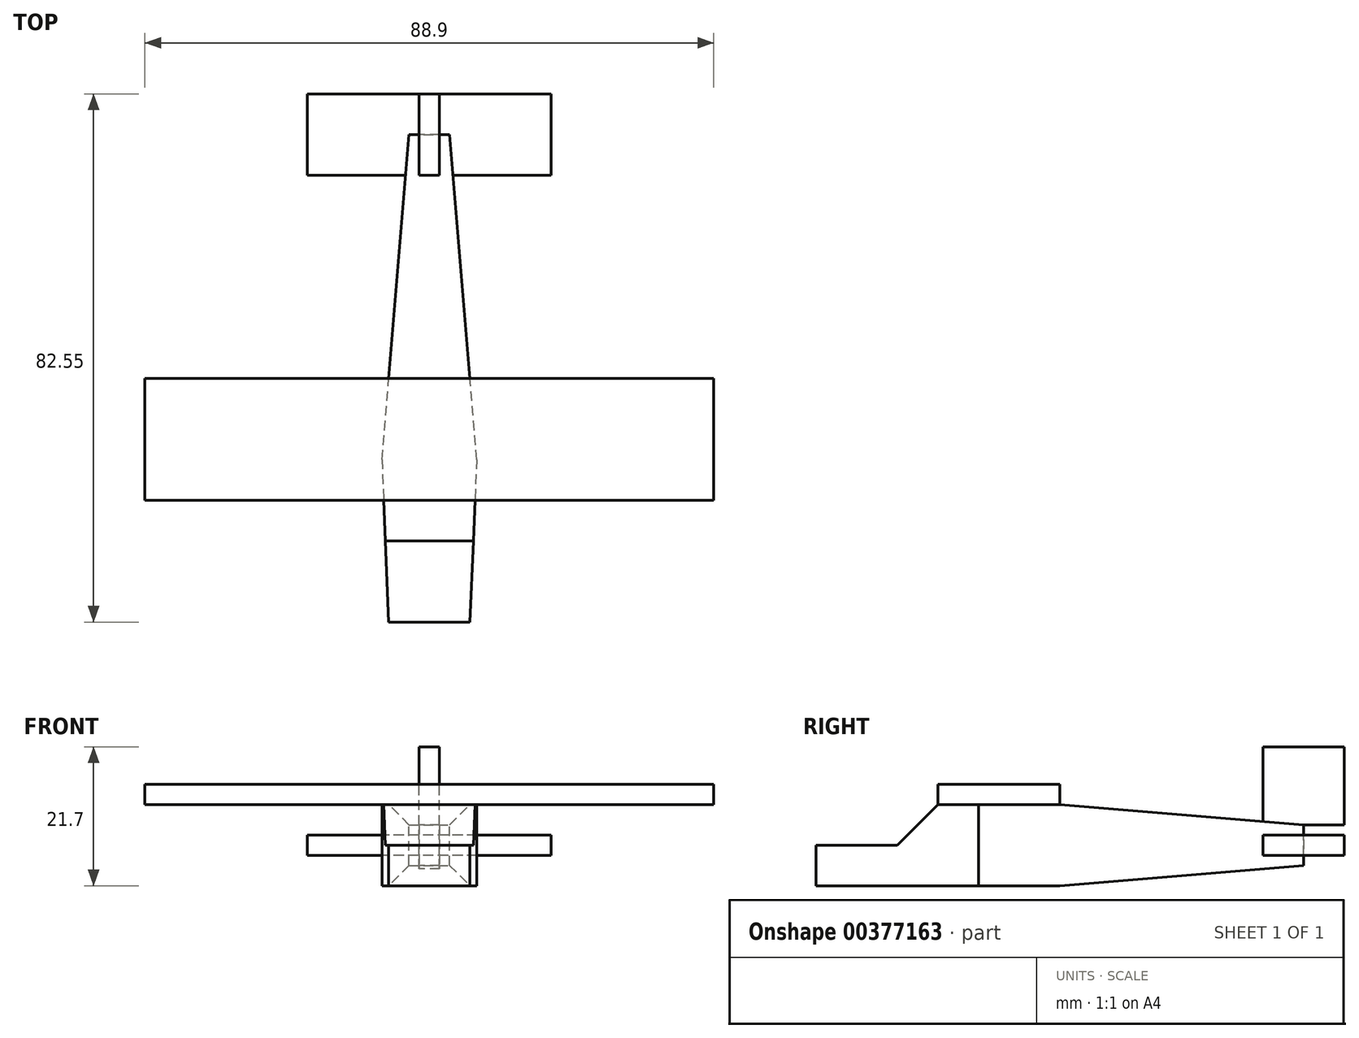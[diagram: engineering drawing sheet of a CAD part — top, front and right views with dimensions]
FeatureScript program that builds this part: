
annotation { "Feature Type Name" : "Feature", "Feature Type Description" : "" }
export const myFeature = defineFeature(function(context is Context, id is Id, definition is map)
    precondition{}
    {
        {
            var Q0;
            Q0=qCreatedBy(makeId("Front.planeOp"),FACE);
            var sketch = newSketch(context, id + "F0", { "sketchPlane" : qUnion([Q0])});
            skLineSegment(sketch, "E0.bottom", {"start": v(9.53, -6.35) * mm, "end": v(-9.53, -6.35) * mm});
            skLineSegment(sketch, "E0.top", {"start": v(9.53, 6.35) * mm, "end": v(-9.53, 6.35) * mm});
            skLineSegment(sketch, "E0.left", {"start": v(9.53, -6.35) * mm, "end": v(9.53, 6.35) * mm});
            skLineSegment(sketch, "E0.right", {"start": v(-9.53, -6.35) * mm, "end": v(-9.53, 6.35) * mm});
            skPoint(sketch, "E0.middle", {"position": v(0, 0) * mm});
            skSolve(sketch);
        }
        {
            var Q0;
            Q0=makeQuery(id+"F0.imprint","IMPRINT",FACE,{"disambiguationData":[TD([[makeQuery(id+"F0.imprint","IMPRINT",EDGE,{"derivedFrom":sQuery(id+"F0.wireOp",EDGE,"E0.bottom")}),-1.0]])]});
            extrude(context, id + "F1", {"entities" : qUnion([Q0]), "depth" : 25.4 * mm, "hasSecondDirection" : true, "secondDirectionOppositeDirection" : true, "secondDirectionDepth" : 50.8 * mm});
        }
        {
            var Q0;
            Q0=makeQuery(id+"F1.opExtrude","SWEPT_FACE",FACE,{"disambiguationData":[OSD([sQuery(id+"F0.wireOp",EDGE,"E0.top")])]});
            var sketch = newSketch(context, id + "F2", { "sketchPlane" : qUnion([Q0])});
            skLineSegment(sketch, "E1", {"start": v(-9.53, -25.4) * mm, "end": v(-3.17, 50.8) * mm});
            skLineSegment(sketch, "E2", {"start": v(-3.17, 50.8) * mm, "end": v(0, 50.8) * mm});
            skLineSegment(sketch, "E3", {"start": v(-9.53, -25.4) * mm, "end": v(0, -25.4) * mm});
            skLineSegment(sketch, "E4.MirrorCS", {"start": v(3.18, 50.8) * mm, "end": v(0, 50.8) * mm});
            skLineSegment(sketch, "E5.MirrorCS", {"start": v(9.53, -25.4) * mm, "end": v(3.17, 50.8) * mm});
            skLineSegment(sketch, "E6.MirrorCS", {"start": v(9.53, -25.4) * mm, "end": v(0, -25.4) * mm});
            skSolve(sketch);
        }
        {
            var Q0;
            Q0=makeQuery(id+"F2.imprint","IMPRINT",FACE,{"disambiguationData":[TD([[makeQuery(id+"F2.imprint","IMPRINT",EDGE,{"derivedFrom":sQuery(id+"F2.wireOp",EDGE,"E1")}),-1.0]])]});
            extrude(context, id + "F3", {"entities" : qUnion([Q0]), "operationType" : NewBodyOperationType.INTERSECT, "endBound" : BoundingType.UP_TO_NEXT, "oppositeDirection" : true, "depth" : 25.4 * mm});
        }
        {
            var Q0;
            Q0=makeQuery(id+"F1.opExtrude","SWEPT_FACE",FACE,{"disambiguationData":[OSD([sQuery(id+"F0.wireOp",EDGE,"E0.top")])]});
            var sketch = newSketch(context, id + "F4", { "sketchPlane" : qUnion([Q0])});
            skLineSegment(sketch, "E7", {"start": v(-7.4, 0) * mm, "end": v(-6.35, -25.4) * mm});
            skLineSegment(sketch, "E8", {"start": v(-7.4, 0) * mm, "end": v(-9.53, -25.4) * mm});
            skLineSegment(sketch, "E9", {"start": v(-9.53, -25.4) * mm, "end": v(-6.35, -25.4) * mm});
            skLineSegment(sketch, "E10.MirrorCS", {"start": v(7.4, 0) * mm, "end": v(6.35, -25.4) * mm});
            skLineSegment(sketch, "E11.MirrorCS", {"start": v(7.4, 0) * mm, "end": v(9.53, -25.4) * mm});
            skLineSegment(sketch, "E12.MirrorCS", {"start": v(9.53, -25.4) * mm, "end": v(6.35, -25.4) * mm});
            skSolve(sketch);
        }
        {
            var Q0;
            Q0=makeQuery(id+"F4.imprint","IMPRINT",FACE,{"disambiguationData":[TD([[makeQuery(id+"F4.imprint","IMPRINT",EDGE,{"derivedFrom":sQuery(id+"F4.wireOp",EDGE,"E7")}),-1.0]])]});
            var Q1;
            Q1=makeQuery(id+"F4.imprint","IMPRINT",FACE,{"disambiguationData":[TD([[makeQuery(id+"F4.imprint","IMPRINT",EDGE,{"derivedFrom":sQuery(id+"F4.wireOp",EDGE,"E10.MirrorCS")}),1.0]])]});
            extrude(context, id + "F5", {"entities" : qUnion([Q0, Q1]), "operationType" : NewBodyOperationType.REMOVE, "endBound" : BoundingType.UP_TO_NEXT, "oppositeDirection" : true, "depth" : 25.4 * mm});
        }
        {
            var Q0;
            Q0=qCreatedBy(makeId("Right.planeOp"),FACE);
            var sketch = newSketch(context, id + "F6", { "sketchPlane" : qUnion([Q0])});
            skLineSegment(sketch, "E13.0", {"start": v(-25.4, -6.35) * mm, "end": v(-25.4, 6.35) * mm, "construction": true});
            skLineSegment(sketch, "E13.1", {"start": v(0, 6.35) * mm, "end": v(-25.4, 6.35) * mm, "construction": true});
            skLineSegment(sketch, "E13.2", {"start": v(0, 6.35) * mm, "end": v(50.8, 6.35) * mm, "construction": true});
            skLineSegment(sketch, "E13.3", {"start": v(50.8, -6.35) * mm, "end": v(50.8, 6.35) * mm, "construction": true});
            skLineSegment(sketch, "E13.4", {"start": v(0, -6.35) * mm, "end": v(50.8, -6.35) * mm, "construction": true});
            skLineSegment(sketch, "E13.5", {"start": v(0, -6.35) * mm, "end": v(-25.4, -6.35) * mm, "construction": true});
            skLineSegment(sketch, "E14", {"start": v(-6.35, 6.35) * mm, "end": v(-12.7, 0) * mm});
            skLineSegment(sketch, "E15", {"start": v(-12.7, 0) * mm, "end": v(-25.4, 0) * mm});
            skLineSegment(sketch, "E16", {"start": v(-25.4, 0) * mm, "end": v(-25.4, 6.35) * mm});
            skLineSegment(sketch, "E17", {"start": v(-6.35, 6.35) * mm, "end": v(-25.4, 6.35) * mm});
            skLineSegment(sketch, "E18", {"start": v(12.7, 6.35) * mm, "end": v(50.8, 3.18) * mm});
            skLineSegment(sketch, "E19", {"start": v(50.8, 3.18) * mm, "end": v(50.8, 6.35) * mm});
            skLineSegment(sketch, "E20", {"start": v(12.7, 6.35) * mm, "end": v(50.8, 6.35) * mm});
            skLineSegment(sketch, "E21", {"start": v(12.7, -6.35) * mm, "end": v(50.8, -3.17) * mm});
            skLineSegment(sketch, "E22", {"start": v(50.8, -3.17) * mm, "end": v(50.8, -6.35) * mm});
            skLineSegment(sketch, "E23", {"start": v(12.7, -6.35) * mm, "end": v(50.8, -6.35) * mm});
            skSolve(sketch);
        }
        {
            var Q0;
            Q0 = qSketchRegion(id + "F6", true);
            extrude(context, id + "F7", {"entities" : qUnion([Q0]), "operationType" : NewBodyOperationType.REMOVE, "endBound" : BoundingType.UP_TO_NEXT, "oppositeDirection" : true, "depth" : 25.4 * mm, "hasSecondDirection" : true, "secondDirectionBound" : SecondDirectionBoundingType.UP_TO_NEXT, "secondDirectionOppositeDirection" : false, "secondDirectionDepth" : 25.4 * mm});
        }
        {
            var Q0;
            Q0=qCreatedBy(makeId("Right.planeOp"),FACE);
            var sketch = newSketch(context, id + "F8", { "sketchPlane" : qUnion([Q0])});
            skLineSegment(sketch, "E24.0", {"start": v(0, 6.35) * mm, "end": v(-6.35, 6.35) * mm, "construction": true});
            skLineSegment(sketch, "E24.1", {"start": v(0, 6.35) * mm, "end": v(12.7, 6.35) * mm, "construction": true});
            skLineSegment(sketch, "E25.bottom", {"start": v(-6.35, 6.35) * mm, "end": v(12.7, 6.35) * mm});
            skLineSegment(sketch, "E25.top", {"start": v(-6.35, 9.53) * mm, "end": v(12.7, 9.53) * mm});
            skLineSegment(sketch, "E25.left", {"start": v(-6.35, 6.35) * mm, "end": v(-6.35, 9.53) * mm});
            skLineSegment(sketch, "E25.right", {"start": v(12.7, 6.35) * mm, "end": v(12.7, 9.53) * mm});
            skSolve(sketch);
        }
        {
            var Q0;
            Q0 = qSketchRegion(id + "F8", true);
            extrude(context, id + "F9", {"entities" : qUnion([Q0]), "endBound" : BoundingType.SYMMETRIC, "depth" : 88.9 * mm});
        }
        {
            var Q0;
            Q0=qCreatedBy(makeId("Top.planeOp"),FACE);
            var sketch = newSketch(context, id + "F10", { "sketchPlane" : qUnion([Q0])});
            skLineSegment(sketch, "E26.0", {"start": v(-3.18, 50.8) * mm, "end": v(3.17, 50.8) * mm, "construction": true});
            skLineSegment(sketch, "E27.bottom", {"start": v(19.05, 57.15) * mm, "end": v(-19.05, 57.15) * mm});
            skLineSegment(sketch, "E27.top", {"start": v(19.05, 44.45) * mm, "end": v(-19.05, 44.45) * mm});
            skLineSegment(sketch, "E27.left", {"start": v(19.05, 57.15) * mm, "end": v(19.05, 44.45) * mm});
            skLineSegment(sketch, "E27.right", {"start": v(-19.05, 57.15) * mm, "end": v(-19.05, 44.45) * mm});
            skPoint(sketch, "E27.middle", {"position": v(0, 50.8) * mm});
            skSolve(sketch);
        }
        {
            var Q0;
            Q0 = qSketchRegion(id + "F10", true);
            extrude(context, id + "F11", {"entities" : qUnion([Q0]), "endBound" : BoundingType.SYMMETRIC, "depth" : 3.17 * mm});
        }
        {
            var Q0;
            Q0=qCreatedBy(makeId("Right.planeOp"),FACE);
            var sketch = newSketch(context, id + "F12", { "sketchPlane" : qUnion([Q0])});
            skLineSegment(sketch, "E28.0", {"start": v(50.8, -3.17) * mm, "end": v(50.8, 3.17) * mm, "construction": true});
            skLineSegment(sketch, "E28.1", {"start": v(50.8, -3.17) * mm, "end": v(12.7, -6.35) * mm, "construction": true});
            skLineSegment(sketch, "E29.0", {"start": v(44.45, 1.59) * mm, "end": v(44.45, -1.59) * mm, "construction": true});
            skLineSegment(sketch, "E30", {"start": v(50.8, -3.17) * mm, "end": v(44.45, -3.7) * mm});
            skLineSegment(sketch, "E31", {"start": v(44.45, -3.7) * mm, "end": v(44.45, 15.35) * mm});
            skPoint(sketch, "E31.endSnap0", {"position": v(44.45, 0) * mm});
            skLineSegment(sketch, "E32", {"start": v(44.45, 15.35) * mm, "end": v(50.8, 15.35) * mm});
            skLineSegment(sketch, "E33", {"start": v(50.8, 3.17) * mm, "end": v(50.8, -3.17) * mm});
            skLineSegment(sketch, "E34", {"start": v(50.8, 3.17) * mm, "end": v(57.15, 3.17) * mm});
            skLineSegment(sketch, "E35", {"start": v(57.15, 3.17) * mm, "end": v(57.15, 15.35) * mm});
            skLineSegment(sketch, "E36", {"start": v(57.15, 15.35) * mm, "end": v(50.8, 15.35) * mm});
            skSolve(sketch);
        }
        {
            var Q0;
            Q0=makeQuery(id+"F12.imprint","IMPRINT",FACE,{"disambiguationData":[TD([[makeQuery(id+"F12.imprint","IMPRINT",EDGE,{"derivedFrom":sQuery(id+"F12.wireOp",EDGE,"E30")}),-1.0]])]});
            extrude(context, id + "F13", {"entities" : qUnion([Q0]), "endBound" : BoundingType.SYMMETRIC, "depth" : 3.17 * mm});
        }
    });
